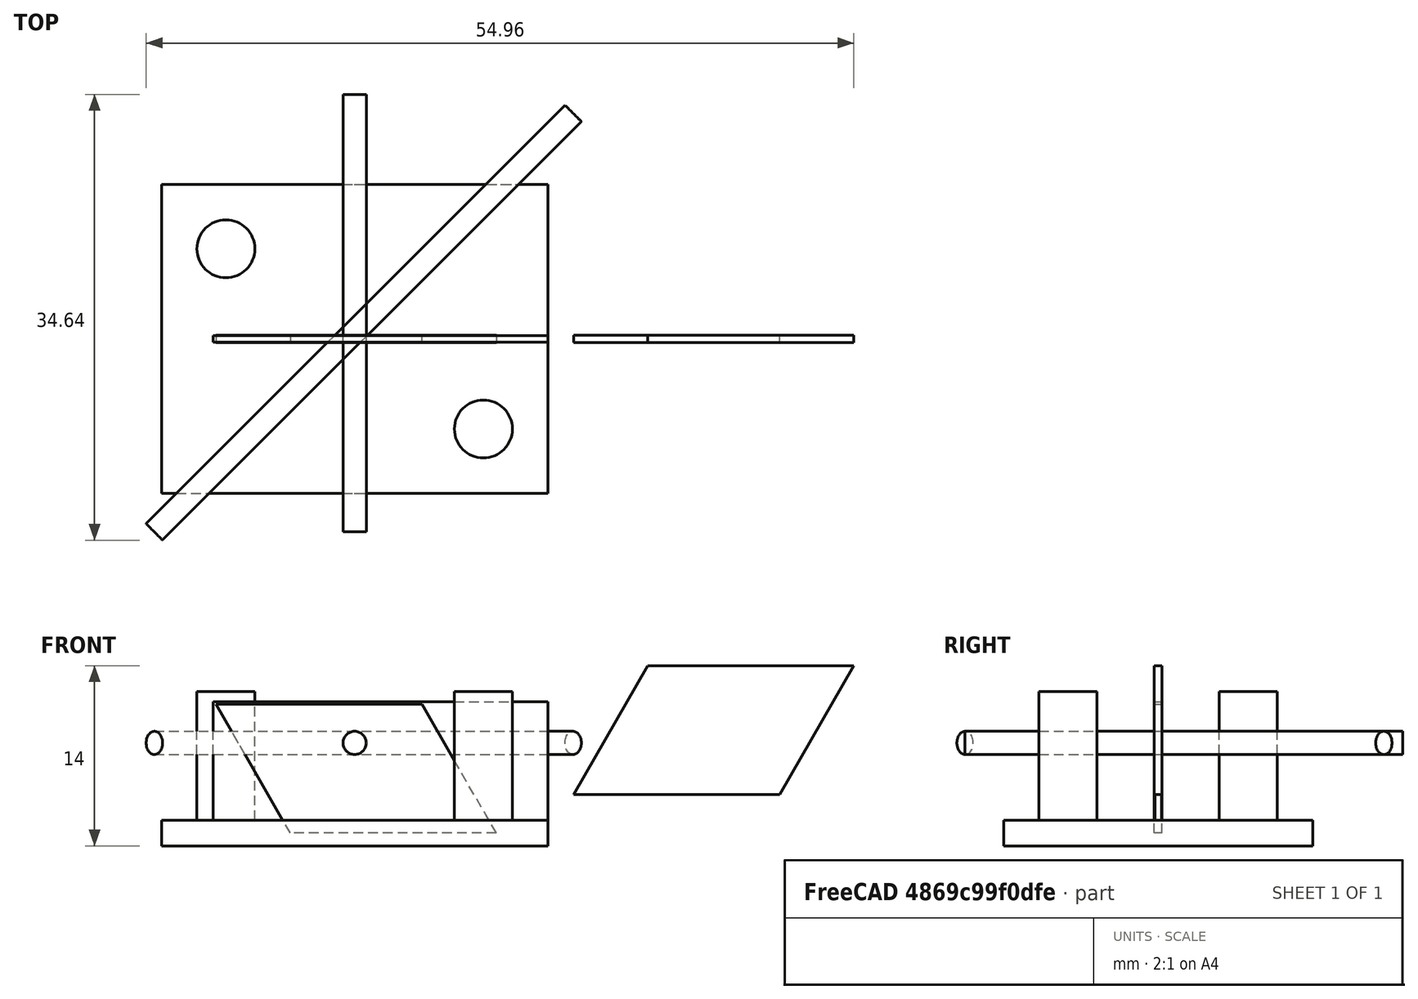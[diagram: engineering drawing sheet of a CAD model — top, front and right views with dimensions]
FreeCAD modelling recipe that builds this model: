
FCSTD DOCUMENT  (FreeCAD 0.18R16146 (Git))
Label: filament-cutter
License: All rights reserved
LicenseURL: http://en.wikipedia.org/wiki/All_rights_reserved
objects: Part::Cylinder×4, Part::Feature×2, Part::Box×2
note: 8 computed .brp shape members not serialized (recipe doc carries the construction recipe); baked Part::Feature solids carry a one-line shape summary decoded from their .brp

FEATURE [Part::Feature] Cut001001  label="blade-slot-001"
  Placement = pos=(2,-0.3,4) rot=(0,0,1;0rad)
  shape: bbox 21.77 x 0.6 x 10 mm, 6 faces (baked)
FEATURE [Part::Cylinder] Cylinder
  Angle = 360
  AttacherType = Attacher::AttachEngine3D
  Height = 10
  Placement = pos=(-25,7,2) rot=(0,0,1;0rad)
  Radius = 2.25
FEATURE [Part::Feature] Cut001001001  label="blade-slot-002"
  Placement = pos=(-2,2e-16,-3) rot=(0,0,1;3.14159rad)
  shape: bbox 21.77 x 0.6 x 10 mm, 6 faces (baked)
FEATURE [Part::Cylinder] Cylinder001
  Angle = 360
  AttacherType = Attacher::AttachEngine3D
  Height = 10
  Placement = pos=(-5,-7,2) rot=(0,0,1;0rad)
  Radius = 2.25
FEATURE [Part::Box] Box  label="Cube"
  AttacherType = Attacher::AttachEngine3D
  Height = 2
  Length = 30
  Placement = pos=(-30,-12,0) rot=(0,0,1;0rad)
  Width = 24
FEATURE [Part::Box] Box001  label="Cube001"
  AttacherType = Attacher::AttachEngine3D
  Height = 9.2
  Length = 26
  Placement = pos=(-26,-0.25,2) rot=(0,0,1;0rad)
  Width = 0.5
FEATURE [Part::Cylinder] Cylinder002
  Angle = 360
  AttacherType = Attacher::AttachEngine3D
  Height = 34
  Placement = pos=(-15,-15,8) rot=(1,0,0;4.71239rad)
  Radius = 0.9
FEATURE [Part::Cylinder] Cylinder003
  Angle = 360
  AttacherType = Attacher::AttachEngine3D
  Height = 46
  Placement = pos=(-30.5563,-15,8) rot=(-0.862856,0.357407,-0.357407;1.71777rad)
  Radius = 0.9
